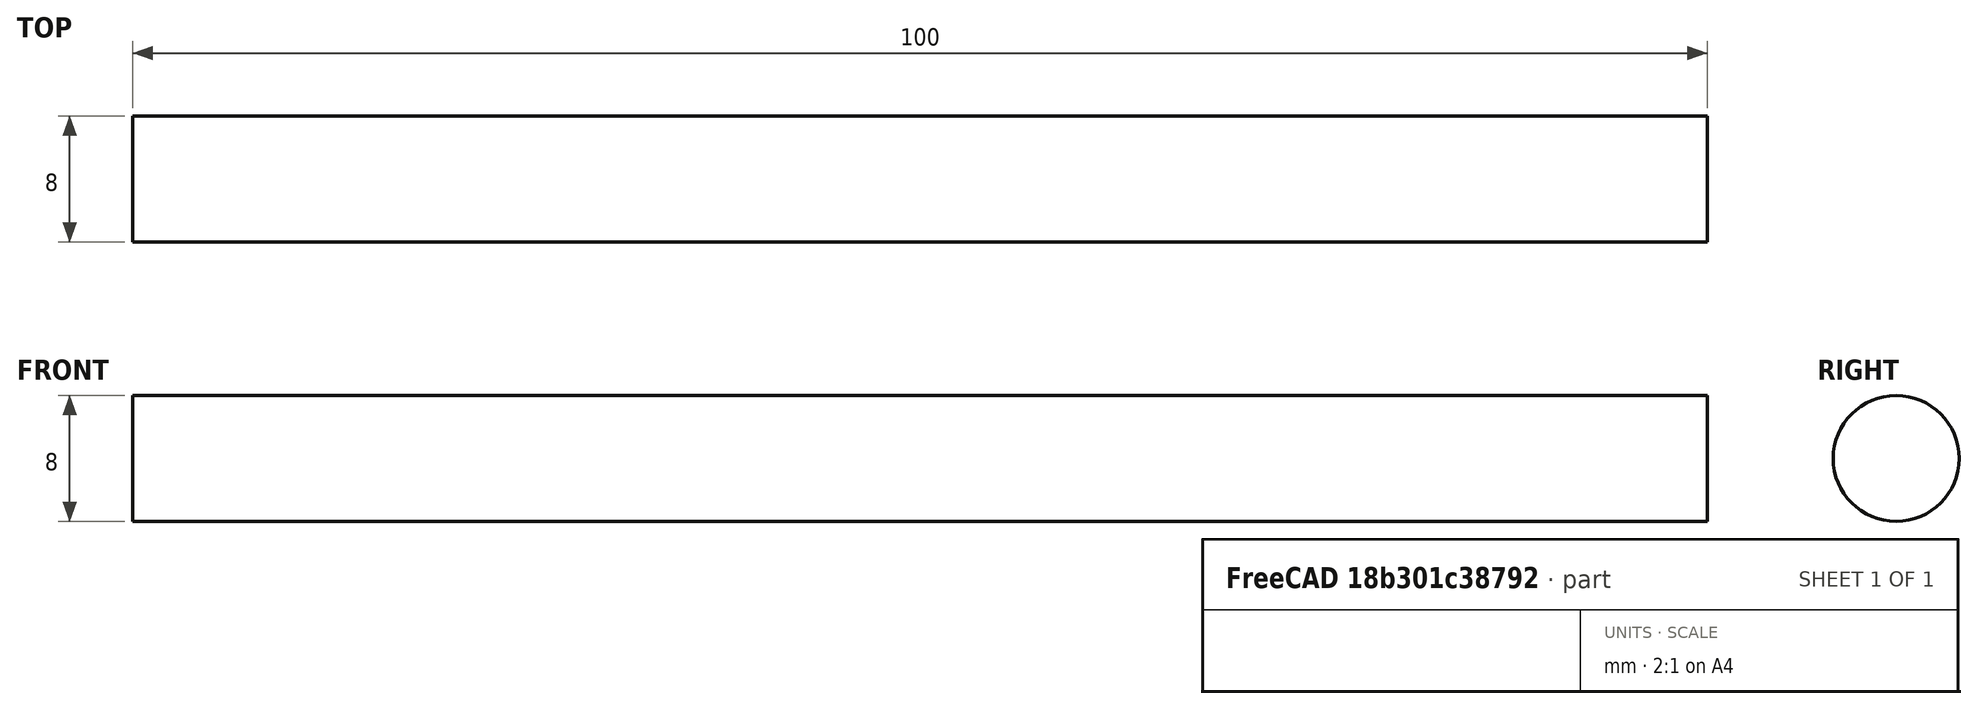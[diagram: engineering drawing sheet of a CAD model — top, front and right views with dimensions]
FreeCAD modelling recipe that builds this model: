
FCSTD DOCUMENT  (FreeCAD 0.18R15969 (Git))
Label: steel-rod
License: All rights reserved
LicenseURL: http://en.wikipedia.org/wiki/All_rights_reserved
objects: Sketcher::SketchObject×1, PartDesign::Pad×1, PartDesign::Body×1
note: 4 computed .brp shape members not serialized (recipe doc carries the construction recipe); baked Part::Feature solids carry a one-line shape summary decoded from their .brp

FEATURE [Sketcher::SketchObject] Sketch
  MapMode = 5
  Placement = pos=(0,0,0) rot=(0.57735,0.57735,0.57735;2.0944rad)
  Support = -> [YZ_Plane]
  sketch-geometry (1):
    g0: Circle CenterX=0 CenterY=0 CenterZ=0 NormalX=0 NormalY=0 NormalZ=1 AngleXU=0 Radius=4
  constraints (2):
    c: Coincident(g0,g-1)
    c: Radius(g0) = 4
FEATURE [PartDesign::Pad] Pad
  Length = 100
  Length2 = 100
  Midplane = true
  Placement = pos=(0,0,0) rot=(0.57735,0.57735,0.57735;2.0944rad)
  Profile = -> Sketch
  Refine = true
  Type = 0
FEATURE [PartDesign::Body] Body
  Group = -> [Sketch,Pad]
  Origin = -> Origin
  Tip = -> Pad
